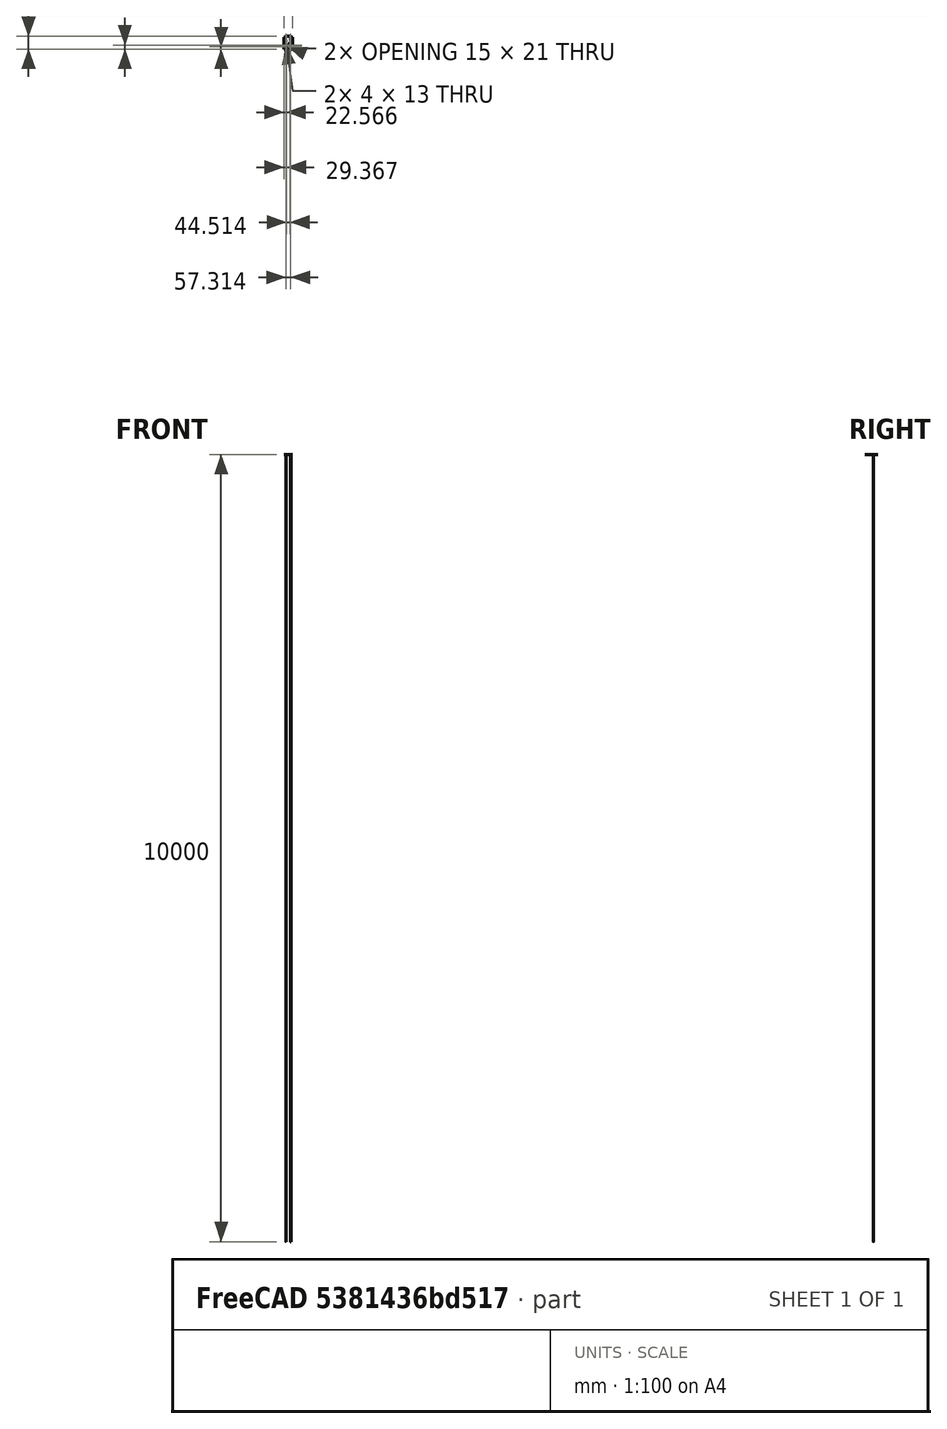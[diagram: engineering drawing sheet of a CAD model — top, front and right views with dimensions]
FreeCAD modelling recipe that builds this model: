
FCSTD DOCUMENT  (FreeCAD 0.16R6704 (Git))
Label: base coche arduino
License: All rights reserved
LicenseURL: http://en.wikipedia.org/wiki/All_rights_reserved
objects: Part::Feature×3, Mesh::Feature×1, Sketcher::SketchObject×1, PartDesign::Pocket×1
note: 6 computed .brp shape members not serialized (recipe doc carries the construction recipe); baked Part::Feature solids carry a one-line shape summary decoded from their .brp

FEATURE [Mesh::Feature] placa_robot  label="placa robot"
FEATURE [Part::Feature] placa_robot001
  shape: bbox 102 x 163.1 x 2.8 mm, 780 faces, 0 solids (baked)
FEATURE [Part::Feature] placa_robot001001  label="placa_robot002"
  shape: bbox 102 x 163.1 x 2.8 mm, 189 faces, 0 solids (baked)
FEATURE [Part::Feature] placa_robot001001_solid  label="placa_robot002 (Solid)"
  shape: bbox 102 x 163.1 x 2.8 mm, 189 faces (baked)
FEATURE [Sketcher::SketchObject] Sketch
  Placement = pos=(0,0,2.8) rot=(0,0,1;0rad)
  Support = -> placa_robot001001_solid [Face1]
  sketch-geometry (2):
    g0: Circle CenterX=-29.6163 CenterY=49.3688 CenterZ=0 NormalX=0 NormalY=0 NormalZ=1 Radius=2
    g1: Circle CenterX=30.0034 CenterY=49.3688 CenterZ=0 NormalX=0 NormalY=0 NormalZ=1 Radius=2
  constraints (2):
    c: Radius(g0) = 2
    c: Radius(g1) = 2
FEATURE [PartDesign::Pocket] Pocket
  Length = 5
  Sketch = -> Sketch
  Type = 1
